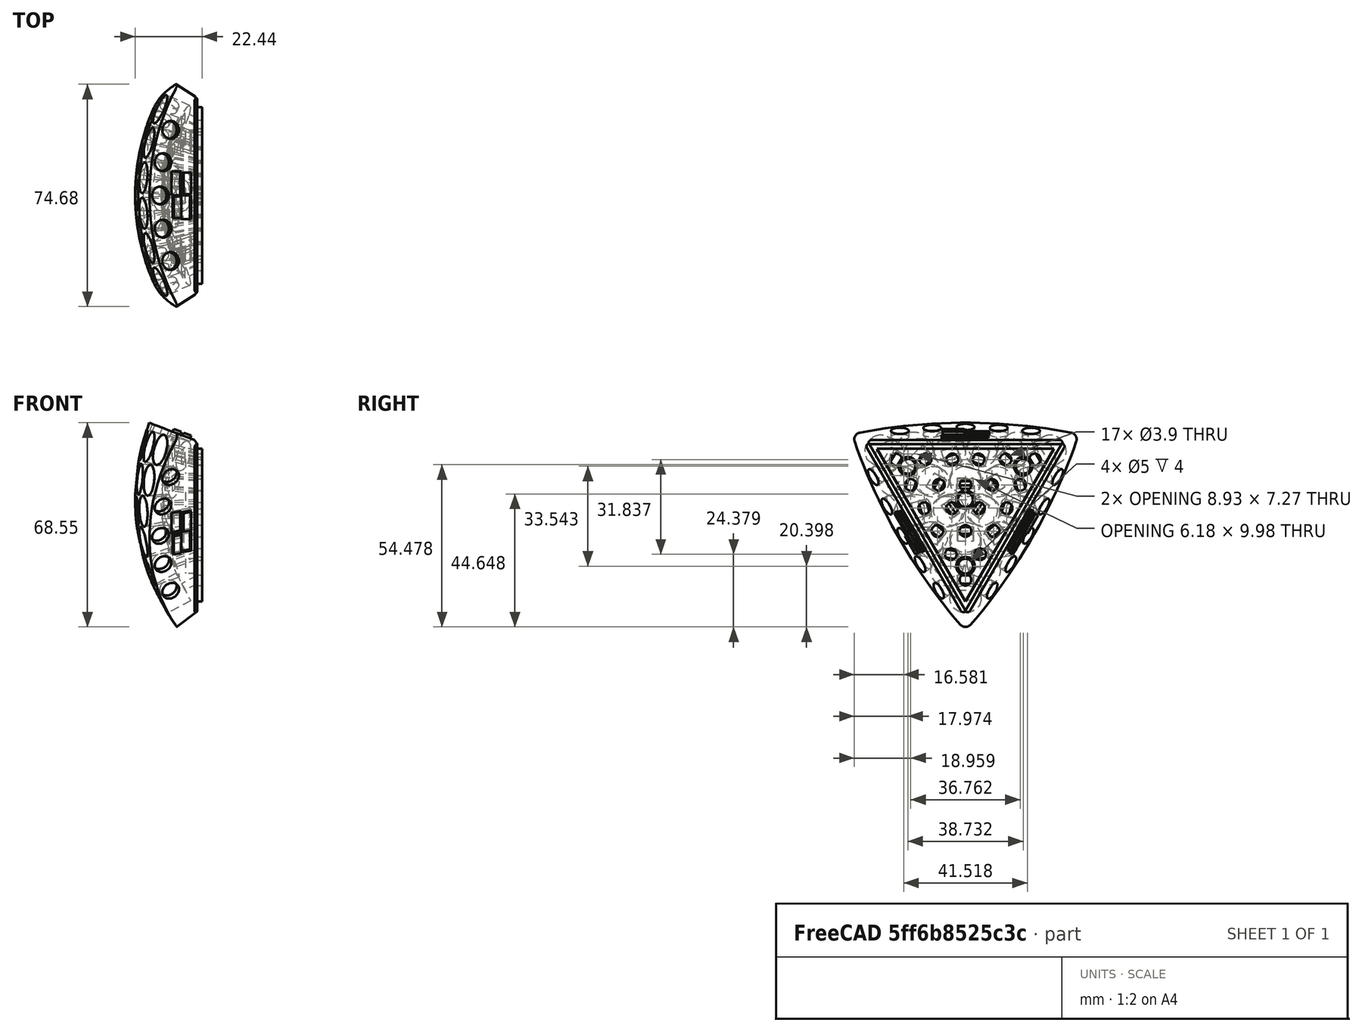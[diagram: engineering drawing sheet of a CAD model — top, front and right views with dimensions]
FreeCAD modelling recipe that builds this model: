
FCSTD DOCUMENT  (FreeCAD 0.20R26720 (Git))
Label: Shell_and_PCB_complete
License: All rights reserved
LicenseURL: http://en.wikipedia.org/wiki/All_rights_reserved
objects: App::FeaturePython×157, Part::FeaturePython×91, Part::Part2DObjectPython×22, App::Link×17, PartDesign::CoordinateSystem×13, Part::Feature×2, Part::Chamfer×1, Part::Fillet×1, PartDesign::FeatureBase×1, PartDesign::Body×1
note: 129 computed .brp shape members not serialized (recipe doc carries the construction recipe); baked Part::Feature solids carry a one-line shape summary decoded from their .brp

FEATURE [Part::Part2DObjectPython] Line  # Draft 2D object (typed FeaturePython)
  Area = 0
  ChamferSize = 0
  Closed = false
  End = (-64.0444,29.0183,16.7537)
  FilletRadius = 0
  Length = 72.2803
  MakeFace = true
  Points = (2) [(0,0,0),(-64.0444,29.0183,16.7537)]
  Start = (0,0,0)
  Subdivisions = 0
FEATURE [Part::Part2DObjectPython] Line001  # Draft 2D object (typed FeaturePython)
  Area = 0
  ChamferSize = 0
  Closed = false
  End = (-67.79,17.7334,17.7336)
  FilletRadius = 0
  Length = 72.2803
  MakeFace = true
  Points = (2) [(0,0,0),(-67.79,17.7334,17.7336)]
  Start = (0,0,0)
  Subdivisions = 0
FEATURE [Part::Part2DObjectPython] Line002  # Draft 2D object (typed FeaturePython)
  Area = 0
  ChamferSize = 0
  Closed = false
  End = (-69.6887,5.9653,18.2302)
  FilletRadius = 0
  Length = 72.2803
  MakeFace = true
  Points = (2) [(0,0,0),(-69.6887,5.9653,18.2302)]
  Start = (0,0,0)
  Subdivisions = 0
FEATURE [Part::Part2DObjectPython] Line003  # Draft 2D object (typed FeaturePython)
  Area = 0
  ChamferSize = 0
  Closed = false
  End = (-69.6887,-5.9653,18.2302)
  FilletRadius = 0
  Length = 72.2803
  MakeFace = true
  Points = (2) [(0,0,0),(-69.6887,-5.9653,18.2302)]
  Start = (0,0,0)
  Subdivisions = 0
FEATURE [Part::Part2DObjectPython] Line004  # Draft 2D object (typed FeaturePython)
  Area = 0
  ChamferSize = 0
  Closed = false
  End = (-67.79,-17.7334,17.7336)
  FilletRadius = 0
  Length = 72.2803
  MakeFace = true
  Points = (2) [(0,0,0),(-67.79,-17.7334,17.7336)]
  Start = (0,0,0)
  Subdivisions = 0
FEATURE [Part::Part2DObjectPython] Line005  # Draft 2D object (typed FeaturePython)
  Area = 0
  ChamferSize = 0
  Closed = false
  End = (-64.0444,-29.0183,16.7537)
  FilletRadius = 0
  Length = 72.2803
  MakeFace = true
  Points = (2) [(0,0,0),(-64.0444,-29.0183,16.7537)]
  Start = (0,0,0)
  Subdivisions = 0
FEATURE [Part::Part2DObjectPython] Line006  # Draft 2D object (typed FeaturePython)
  Area = 0
  ChamferSize = 0
  Closed = false
  End = (-67.79,24.2244,6.49078)
  FilletRadius = 0
  Length = 72.2803
  MakeFace = true
  Points = (2) [(0,0,0),(-67.79,24.2244,6.49078)]
  Start = (0,0,0)
  Subdivisions = 0
FEATURE [Part::Part2DObjectPython] Line007  # Draft 2D object (typed FeaturePython)
  Area = 0
  ChamferSize = 0
  Closed = false
  End = (-70.9033,12.2912,6.78887)
  FilletRadius = 0
  Length = 72.2803
  MakeFace = true
  Points = (2) [(0,0,0),(-70.9033,12.2912,6.78887)]
  Start = (0,0,0)
  Subdivisions = 0
FEATURE [Part::Part2DObjectPython] Line008  # Draft 2D object (typed FeaturePython)
  Area = 0
  ChamferSize = 0
  Closed = false
  End = (-71.9512,-1.03e-14,6.8892)
  FilletRadius = 0
  Length = 72.2803
  MakeFace = true
  Points = (2) [(0,0,0),(-71.9512,-1.02696e-14,6.8892)]
  Start = (0,0,0)
  Subdivisions = 0
FEATURE [Part::Part2DObjectPython] Line009  # Draft 2D object (typed FeaturePython)
  Area = 0
  ChamferSize = 0
  Closed = false
  End = (-70.9033,-12.2912,6.78887)
  FilletRadius = 0
  Length = 72.2803
  MakeFace = true
  Points = (2) [(0,0,0),(-70.9033,-12.2912,6.78887)]
  Start = (0,0,0)
  Subdivisions = 0
FEATURE [Part::Part2DObjectPython] Line010  # Draft 2D object (typed FeaturePython)
  Area = 0
  ChamferSize = 0
  Closed = false
  End = (-67.79,-24.2244,6.49078)
  FilletRadius = 0
  Length = 72.2803
  MakeFace = true
  Points = (2) [(0,0,0),(-67.79,-24.2244,6.49078)]
  Start = (0,0,0)
  Subdivisions = 0
FEATURE [Part::Part2DObjectPython] Line011  # Draft 2D object (typed FeaturePython)
  Area = 0
  ChamferSize = 0
  Closed = false
  End = (-69.6887,18.7705,-3.94902)
  FilletRadius = 0
  Length = 72.2803
  MakeFace = true
  Points = (2) [(0,0,0),(-69.6887,18.7705,-3.94902)]
  Start = (0,0,0)
  Subdivisions = 0
FEATURE [Part::Part2DObjectPython] Line012  # Draft 2D object (typed FeaturePython)
  Area = 0
  ChamferSize = 0
  Closed = false
  End = (-71.888,6.3213,-4.07365)
  FilletRadius = 0
  Length = 72.2803
  MakeFace = true
  Points = (2) [(0,0,0),(-71.888,6.3213,-4.07365)]
  Start = (0,0,0)
  Subdivisions = 0
FEATURE [Part::Part2DObjectPython] Line013  # Draft 2D object (typed FeaturePython)
  Area = 0
  ChamferSize = 0
  Closed = false
  End = (-71.888,-6.3213,-4.07365)
  FilletRadius = 0
  Length = 72.2803
  MakeFace = true
  Points = (2) [(0,0,0),(-71.888,-6.3213,-4.07365)]
  Start = (0,0,0)
  Subdivisions = 0
FEATURE [Part::Part2DObjectPython] Line014  # Draft 2D object (typed FeaturePython)
  Area = 0
  ChamferSize = 0
  Closed = false
  End = (-69.6887,-18.7705,-3.94902)
  FilletRadius = 0
  Length = 72.2803
  MakeFace = true
  Points = (2) [(0,0,0),(-69.6887,-18.7705,-3.94902)]
  Start = (0,0,0)
  Subdivisions = 0
FEATURE [Part::Part2DObjectPython] Line015  # Draft 2D object (typed FeaturePython)
  Area = 0
  ChamferSize = 0
  Closed = false
  End = (-69.6887,12.8052,-14.2812)
  FilletRadius = 0
  Length = 72.2803
  MakeFace = true
  Points = (2) [(0,0,0),(-69.6887,12.8052,-14.2812)]
  Start = (0,0,0)
  Subdivisions = 0
FEATURE [Part::Part2DObjectPython] Line016  # Draft 2D object (typed FeaturePython)
  Area = 0
  ChamferSize = 0
  Closed = false
  End = (-70.8088,7.7e-15,-14.5108)
  FilletRadius = 0
  Length = 72.2803
  MakeFace = true
  Points = (2) [(0,0,0),(-70.8088,7.66054e-15,-14.5108)]
  Start = (0,0,0)
  Subdivisions = 0
FEATURE [Part::Part2DObjectPython] Line017  # Draft 2D object (typed FeaturePython)
  Area = 0
  ChamferSize = 0
  Closed = false
  End = (-69.6887,-12.8052,-14.2812)
  FilletRadius = 0
  Length = 72.2803
  MakeFace = true
  Points = (2) [(0,0,0),(-69.6887,-12.8052,-14.2812)]
  Start = (0,0,0)
  Subdivisions = 0
FEATURE [Part::Part2DObjectPython] Line018  # Draft 2D object (typed FeaturePython)
  Area = 0
  ChamferSize = 0
  Closed = false
  End = (-67.79,6.49102,-24.2243)
  FilletRadius = 0
  Length = 72.2803
  MakeFace = true
  Points = (2) [(0,0,0),(-67.79,6.49102,-24.2243)]
  Start = (0,0,0)
  Subdivisions = 0
FEATURE [Part::Part2DObjectPython] Line019  # Draft 2D object (typed FeaturePython)
  Area = 0
  ChamferSize = 0
  Closed = false
  End = (-67.79,-6.49102,-24.2243)
  FilletRadius = 0
  Length = 72.2803
  MakeFace = true
  Points = (2) [(0,0,0),(-67.79,-6.49102,-24.2243)]
  Start = (0,0,0)
  Subdivisions = 0
FEATURE [Part::Part2DObjectPython] Line020  # Draft 2D object (typed FeaturePython)
  Area = 0
  ChamferSize = 0
  Closed = false
  End = (-64.0444,1.8e-15,-33.5075)
  FilletRadius = 0
  Length = 72.2803
  MakeFace = true
  Points = (2) [(0,0,0),(-64.0444,1.77636e-15,-33.5075)]
  Start = (0,0,0)
  Subdivisions = 0
FEATURE [Part::Part2DObjectPython] Line021  # Draft 2D object (typed FeaturePython)
  Area = 0
  ChamferSize = 0
  Closed = false
  End = (-57.4379,0,6.2e-15)
  FilletRadius = 0
  Length = 57.4379
  MakeFace = true
  Points = (2) [(0,0,0),(-57.4379,0,6.20075e-15)]
  Start = (0,0,0)
  Subdivisions = 0
FEATURE [Part::Feature] Shape
  shape: bbox 24.38 x 79.76 x 69.75 mm, 229 faces (baked)
FEATURE [Part::Feature] Shape001
  shape: bbox 1.6 x 59.35 x 51.4 mm, 36 faces (baked)
FEATURE [Part::Chamfer] Chamfer
  Base = -> Shape
  Edges = 3 edges r=1: [Edge26,Edge49,Edge72]
FEATURE [Part::Fillet] Fillet
  Base = -> Chamfer
  Edges = 3 edges r=2: [Edge1,Edge4,Edge27]
FEATURE [PartDesign::FeatureBase] BaseFeature
  BaseFeature = -> Fillet
FEATURE [PartDesign::CoordinateSystem] Local_CS
  AttacherType = Attacher::AttachEngine3D
  MapMode = 11
  Placement = pos=(-63.7856,-7e-15,24.3639) rot=(0.701166,0.701166,-0.129353;3.39887rad)
  Support = -> [BaseFeature]
FEATURE [PartDesign::CoordinateSystem] Local_CS001
  AttacherType = Attacher::AttachEngine3D
  MapMode = 11
  Placement = pos=(-63.7856,-21.0998,-12.182) rot=(-0.317298,-0.615291,-0.721622;1.68298rad)
  Support = -> [BaseFeature]
FEATURE [PartDesign::CoordinateSystem] Local_CS002
  AttacherType = Attacher::AttachEngine3D
  MapMode = 11
  Placement = pos=(-63.7856,21.0998,-12.182) rot=(0.544291,0.280684,-0.790546;2.00531rad)
  Support = -> [BaseFeature]
FEATURE [PartDesign::CoordinateSystem] Local_CS003
  AttacherType = Attacher::AttachEngine3D
  MapMode = 11
  Placement = pos=(-60.3757,8.95889,-30.6057) rot=(0.544291,0.280684,-0.790546;2.00531rad)
  Support = -> [BaseFeature]
FEATURE [PartDesign::CoordinateSystem] Local_CS004
  AttacherType = Attacher::AttachEngine3D
  MapMode = 11
  Placement = pos=(-60.3757,30.9848,7.54423) rot=(0.544291,0.280684,-0.790546;2.00531rad)
  Support = -> [BaseFeature]
FEATURE [PartDesign::CoordinateSystem] Local_CS005
  AttacherType = Attacher::AttachEngine3D
  MapMode = 11
  Placement = pos=(-60.3757,-8.95889,-30.6057) rot=(-0.317298,-0.615291,-0.721622;1.68298rad)
  Support = -> [BaseFeature]
FEATURE [PartDesign::CoordinateSystem] Local_CS006
  AttacherType = Attacher::AttachEngine3D
  MapMode = 11
  Placement = pos=(-60.3757,-30.9848,7.54423) rot=(-0.317298,-0.615291,-0.721622;1.68298rad)
  Support = -> [BaseFeature]
FEATURE [PartDesign::CoordinateSystem] Local_CS007
  AttacherType = Attacher::AttachEngine3D
  MapMode = 11
  Placement = pos=(-60.3757,-22.0259,23.0615) rot=(0.701166,0.701166,-0.129353;3.39887rad)
  Support = -> [BaseFeature]
FEATURE [PartDesign::CoordinateSystem] Local_CS008
  AttacherType = Attacher::AttachEngine3D
  MapMode = 11
  Placement = pos=(-60.3757,22.0259,23.0615) rot=(0.701166,0.701166,-0.129353;3.39887rad)
  Support = -> [BaseFeature]
FEATURE [PartDesign::CoordinateSystem] Local_CS009
  AttacherType = Attacher::AttachEngine3D
  MapMode = 11
  Placement = pos=(-51.4379,-19.3661,11.181) rot=(0.57735,0.57735,-0.57735;4.18879rad)
  Support = -> [BaseFeature]
FEATURE [PartDesign::CoordinateSystem] Local_CS010
  AttacherType = Attacher::AttachEngine3D
  MapMode = 11
  Placement = pos=(-51.4379,19.3661,11.181) rot=(0.57735,0.57735,-0.57735;4.18879rad)
  Support = -> [BaseFeature]
FEATURE [PartDesign::CoordinateSystem] Local_CS011
  AttacherType = Attacher::AttachEngine3D
  MapMode = 11
  Placement = pos=(-51.4379,0,-22.362) rot=(0.57735,0.57735,-0.57735;4.18879rad)
  Support = -> [BaseFeature]
FEATURE [PartDesign::CoordinateSystem] Local_CS012
  AttacherType = Attacher::AttachEngine3D
  MapMode = 11
  Placement = pos=(-51.4379,2e-15,1.69e-14) rot=(0.57735,0.57735,-0.57735;4.18879rad)
  Support = -> [BaseFeature]
FEATURE [PartDesign::Body] Body  label="shell"
  BaseFeature = -> Fillet
  Group = -> [BaseFeature,Local_CS,Local_CS001,Local_CS002,Local_CS003,Local_CS004,Local_CS005,Local_CS006,Local_CS007,Local_CS008,Local_CS009,Local_CS010,Local_CS011,Local_CS012]
  Origin = -> Origin
  Tip = -> BaseFeature
FEATURE [App::Link] Link  label="shell001"
  LinkedObject = -> Body
FEATURE [App::Link] Link001  label="shell002"
  LinkPlacement = pos=(7.7e-15,-5.52e-14,-1.103e-13) rot=(0.934172,-0.309017,0.178411;3.14159rad)
  LinkedObject = -> Body
  Placement = pos=(7.7e-15,-5.52e-14,-1.103e-13) rot=(0.934172,-0.309017,0.178411;3.14159rad)
FEATURE [App::Link] Link002  label="shell003"
  LinkPlacement = pos=(-1.36941e-09,6.11616e-09,3.09893e-09) rot=(0.794654,0.525731,-0.303531;1.25664rad)
  LinkedObject = -> Body
  Placement = pos=(-1.36941e-09,6.11616e-09,3.09893e-09) rot=(0.794654,0.525731,-0.303531;1.25664rad)
FEATURE [App::Link] Link003  label="shell004"
  LinkPlacement = pos=(-4.2003e-10,6.96406e-09,3.62865e-09) rot=(0.187592,0.850651,0.491123;1.25664rad)
  LinkedObject = -> Body
  Placement = pos=(-4.2003e-10,6.96406e-09,3.62865e-09) rot=(0.187592,0.850651,0.491123;1.25664rad)
FEATURE [App::Link] Link004  label="shell005"
  LinkPlacement = pos=(4.384e-12,-1.7666e-12,-5.0822e-12) rot=(0.745356,-0.57735,0.333333;2.0944rad)
  LinkedObject = -> Body
  Placement = pos=(4.384e-12,-1.7666e-12,-5.0822e-12) rot=(0.745356,-0.57735,0.333333;2.0944rad)
FEATURE [App::Link] Link005  label="shell006"
  LinkPlacement = pos=(-8.70131e-10,6.80711e-09,3.59799e-09) rot=(0.333333,0.934172,-0.127322;2.0944rad)
  LinkedObject = -> Body
  Placement = pos=(-8.70131e-10,6.80711e-09,3.59799e-09) rot=(0.333333,0.934172,-0.127322;2.0944rad)
FEATURE [App::Link] Link006  label="shell007"
  LinkPlacement = pos=(2.09781e-10,-2.78995e-11,-1.62592e-10) rot=(0.333333,-0.934172,-0.127322;2.0944rad)
  LinkedObject = -> Body
  Placement = pos=(2.09781e-10,-2.78995e-11,-1.62592e-10) rot=(0.333333,-0.934172,-0.127322;2.0944rad)
FEATURE [App::Link] Link007  label="shell008"
  LinkPlacement = pos=(-8.88912e-10,6.80266e-09,3.49688e-09) rot=(0.356822,0.809017,-0.467086;3.14159rad)
  LinkedObject = -> Body
  Placement = pos=(-8.88912e-10,6.80266e-09,3.49688e-09) rot=(0.356822,0.809017,-0.467086;3.14159rad)
FEATURE [App::Link] Link008  label="shell009"
  LinkPlacement = pos=(-5.90248e-10,-4.7757e-10,-1.80727e-09) rot=(0.356822,0,0.934172;3.14159rad)
  LinkedObject = -> Body
  Placement = pos=(-5.90248e-10,-4.7757e-10,-1.80727e-09) rot=(0.356822,0,0.934172;3.14159rad)
FEATURE [App::Link] Link009  label="shell010"
  LinkPlacement = pos=(-8.90973e-10,6.86674e-10,-1.59251e-09) rot=(0,-0.5,0.866025;3.14159rad)
  LinkedObject = -> Body
  Placement = pos=(-8.90973e-10,6.86674e-10,-1.59251e-09) rot=(0,-0.5,0.866025;3.14159rad)
FEATURE [Part::FeaturePython] Parts  # WARN: FeaturePython — macro-defined, semantics opaque (R4)
  Group = -> [Link001,Link,Link002,Link003,Link004,Link005,Link006,Link007,Link008,Link009]
  GroupMode = 0
FEATURE [App::Link] Link010  label="shell011"
  LinkPlacement = pos=(8.96105,1.2242e-07,11.0286) rot=(0,1,0;0.31747rad)
  LinkedObject = -> Body
  Placement = pos=(8.96105,1.2242e-07,11.0286) rot=(0,1,0;0.31747rad)
FEATURE [App::Link] Link011  label="shell012"
  LinkPlacement = pos=(8.96105,1.22409e-07,11.0286) rot=(0.654654,0.654654,-0.377965;1.44547rad)
  LinkedObject = -> Body
  Placement = pos=(8.96105,1.22409e-07,11.0286) rot=(0.654654,0.654654,-0.377965;1.44547rad)
FEATURE [App::Link] Link012  label="shell013"
  LinkPlacement = pos=(8.96105,1.22266e-07,11.0286) rot=(-0.816253,-0.334129,0.471264;1.11835rad)
  LinkedObject = -> Body
  Placement = pos=(8.96105,1.22266e-07,11.0286) rot=(-0.816253,-0.334129,0.471264;1.11835rad)
FEATURE [App::Link] Link013  label="shell014"
  LinkPlacement = pos=(8.96105,1.22267e-07,11.0286) rot=(-0.029286,0.21259,0.976702;1.29084rad)
  LinkedObject = -> Body
  Placement = pos=(8.96105,1.22267e-07,11.0286) rot=(-0.029286,0.21259,0.976702;1.29084rad)
FEATURE [App::Link] Link014  label="shell015"
  LinkPlacement = pos=(8.96105,1.22248e-07,11.0286) rot=(0.22258,0.895451,0.38552;1.53453rad)
  LinkedObject = -> Body
  Placement = pos=(8.96105,1.22248e-07,11.0286) rot=(0.22258,0.895451,0.38552;1.53453rad)
FEATURE [Part::FeaturePython] Parts001  # WARN: FeaturePython — macro-defined, semantics opaque (R4)
  Group = -> [Link010,Link011,Link012,Link013,Link014]
  GroupMode = 0
FEATURE [App::Link] Link015  label="Ring Assembly001"
  LinkPlacement = pos=(6.33641,-16.0136,1.7045) rot=(-0.868596,-0.489826,0.074905;0.379444rad)
  LinkedObject = -> Assembly
  Placement = pos=(6.33641,-16.0136,1.7045) rot=(-0.868596,-0.489826,0.074905;0.379444rad)
FEATURE [App::Link] Link016  label="Circle Assembly001"
  LinkPlacement = pos=(-8.99333e-06,-12.6957,-10.5744) rot=(0.678598,-0.281085,0.678598;1.09606rad)
  LinkedObject = -> Assembly001
  Placement = pos=(-8.99333e-06,-12.6957,-10.5744) rot=(0.678598,-0.281085,0.678598;1.09606rad)
FEATURE [Part::FeaturePython] Parts002  # WARN: FeaturePython — macro-defined, semantics opaque (R4)
  Group = -> [Link015,Link016]
  GroupMode = 0
FEATURE [Part::FeaturePython] Assembly  label="Ring Assembly"  # WARN: FeaturePython — macro-defined, semantics opaque (R4)
  AutoRelax = true
  BuildShape = 0
  Freeze = false
  Group = -> [Constraints,Elements,Parts]
  Verbose = false
  _SolverType = 1
  _Version = 1
FEATURE [App::FeaturePython] Constraints  # WARN: FeaturePython — macro-defined, semantics opaque (R4)
  Group = -> [Constraint,Constraint001,Constraint002,Constraint003,Constraint004,Constraint005,Constraint006,Constraint008,Constraint010,Constraint011,Constraint012,Constraint013,Constraint014,Constraint015,Constraint016,Constraint017,Constraint018,Constraint019,Constraint020,Constraint021,Constraint022,Constraint023,Constraint024,Constraint025,Constraint026,Constraint027,Constraint028,Constraint029,+6 more]
  _Version = 1
FEATURE [App::FeaturePython] Elements  # WARN: FeaturePython — macro-defined, semantics opaque (R4)
  Group = -> [_Element,_Element001,_Element002,_Element003,_Element004,_Element005,_Element006,_Element007,_Element008,_Element009,_Element010,_Element011,_Element012,_Element013,_Element015,_Element017,_Element019,_Element020,_Element021,_Element022,_Element023,_Element024,_Element025,_Element026,_Element027,_Element028,_Element029,_Element030,_Element031,_Element032,_Element033,_Element034,_Element035,+25 more]
FEATURE [App::FeaturePython] Constraint  label="AxialAlignment"  # WARN: FeaturePython — macro-defined, semantics opaque (R4)
  Angle = 0
  AnglePitch = 0
  AngleRoll = 0
  Disabled = false
  Group = -> [ElementLink,ElementLink001]
  LockAngle = false
  Multiply = false
  _ConstraintType = 36
  _Parent = -> Constraints
FEATURE [App::FeaturePython] ElementLink  label="_Element"  # link proxy (typed FeaturePython)
  LinkTransform = true
  LinkedObject = -> _Element
  _Parent = -> Constraint
FEATURE [Part::FeaturePython] _Element  # link proxy (typed FeaturePython)
  Detach = false
  LinkTransform = true
  LinkedObject = -> Link [BaseFeature.Edge218]
  _Parent = -> Elements
FEATURE [App::FeaturePython] ElementLink001  label="_Element001"  # link proxy (typed FeaturePython)
  LinkTransform = true
  LinkedObject = -> _Element001
  _Parent = -> Constraint
FEATURE [Part::FeaturePython] _Element001  # link proxy (typed FeaturePython)
  Detach = false
  LinkTransform = true
  LinkedObject = -> Link001 [BaseFeature.Edge198]
  _Parent = -> Elements
FEATURE [App::FeaturePython] Constraint001  label="AxialAlignment001"  # WARN: FeaturePython — macro-defined, semantics opaque (R4)
  Angle = 0
  AnglePitch = 0
  AngleRoll = 0
  Disabled = false
  Group = -> [ElementLink002,ElementLink003]
  LockAngle = false
  Multiply = false
  _ConstraintType = 36
  _Parent = -> Constraints
FEATURE [App::FeaturePython] ElementLink002  label="_Element002"  # link proxy (typed FeaturePython)
  LinkTransform = true
  LinkedObject = -> _Element002
  _Parent = -> Constraint001
FEATURE [Part::FeaturePython] _Element002  # link proxy (typed FeaturePython)
  Detach = false
  LinkTransform = true
  LinkedObject = -> Link [BaseFeature.Edge198]
  _Parent = -> Elements
FEATURE [App::FeaturePython] ElementLink003  label="_Element003"  # link proxy (typed FeaturePython)
  LinkTransform = true
  LinkedObject = -> _Element003
  _Parent = -> Constraint001
FEATURE [Part::FeaturePython] _Element003  # link proxy (typed FeaturePython)
  Detach = false
  LinkTransform = true
  LinkedObject = -> Link001 [BaseFeature.Edge218]
  _Parent = -> Elements
FEATURE [Part::FeaturePython] _Element004  # link proxy (typed FeaturePython)
  Detach = false
  LinkTransform = true
  LinkedObject = -> Link001 [BaseFeature.Face30]
  _Parent = -> Elements
FEATURE [Part::FeaturePython] _Element005  # link proxy (typed FeaturePython)
  Detach = false
  LinkTransform = true
  LinkedObject = -> Link [BaseFeature.Face30]
  _Parent = -> Elements
FEATURE [App::FeaturePython] Constraint002  label="PlaneCoincident"  # WARN: FeaturePython — macro-defined, semantics opaque (R4)
  Angle = 0
  AnglePitch = 0
  AngleRoll = 0
  Cascade = false
  Disabled = false
  Group = -> [ElementLink004,ElementLink005]
  LockAngle = false
  Multiply = false
  OffsetX = 0
  OffsetY = 0
  _ConstraintType = 35
  _Parent = -> Constraints
FEATURE [App::FeaturePython] ElementLink004  label="_Element006"  # link proxy (typed FeaturePython)
  LinkTransform = true
  LinkedObject = -> _Element006
  _Parent = -> Constraint002
FEATURE [Part::FeaturePython] _Element006  # link proxy (typed FeaturePython)
  Detach = false
  LinkTransform = true
  LinkedObject = -> Link [BaseFeature.Edge209]
  _Parent = -> Elements
FEATURE [App::FeaturePython] ElementLink005  label="_Element007"  # link proxy (typed FeaturePython)
  LinkTransform = true
  LinkedObject = -> _Element007
  _Parent = -> Constraint002
FEATURE [Part::FeaturePython] _Element007  # link proxy (typed FeaturePython)
  Detach = false
  LinkTransform = true
  LinkedObject = -> Link001 [BaseFeature.Edge199]
  _Parent = -> Elements
FEATURE [App::FeaturePython] Constraint003  label="AxialAlignment002"  # WARN: FeaturePython — macro-defined, semantics opaque (R4)
  Angle = 0
  AnglePitch = 0
  AngleRoll = 0
  Disabled = true
  Group = -> [ElementLink006,ElementLink007]
  LockAngle = false
  Multiply = false
  _ConstraintType = 36
  _Parent = -> Constraints
FEATURE [App::FeaturePython] ElementLink006  label="_Element008"  # link proxy (typed FeaturePython)
  LinkTransform = true
  LinkedObject = -> _Element008
  _Parent = -> Constraint003
FEATURE [Part::FeaturePython] _Element008  # link proxy (typed FeaturePython)
  Detach = false
  LinkTransform = true
  LinkedObject = -> Link [BaseFeature.Edge240]
  _Parent = -> Elements
FEATURE [App::FeaturePython] ElementLink007  label="_Element009"  # link proxy (typed FeaturePython)
  LinkTransform = true
  LinkedObject = -> _Element009
  _Parent = -> Constraint003
FEATURE [Part::FeaturePython] _Element009  # link proxy (typed FeaturePython)
  Detach = false
  LinkTransform = true
  LinkedObject = -> Link002 [BaseFeature.Edge17]
  _Parent = -> Elements
FEATURE [App::FeaturePython] Constraint004  label="AxialAlignment003"  # WARN: FeaturePython — macro-defined, semantics opaque (R4)
  Angle = 0
  AnglePitch = 0
  AngleRoll = 0
  Disabled = true
  Group = -> [ElementLink008,ElementLink009]
  LockAngle = false
  Multiply = false
  _ConstraintType = 36
  _Parent = -> Constraints
FEATURE [App::FeaturePython] ElementLink008  label="_Element010"  # link proxy (typed FeaturePython)
  LinkTransform = true
  LinkedObject = -> _Element010
  _Parent = -> Constraint004
FEATURE [Part::FeaturePython] _Element010  # link proxy (typed FeaturePython)
  Detach = false
  LinkTransform = true
  LinkedObject = -> Link002 [BaseFeature.Edge6]
  _Parent = -> Elements
FEATURE [App::FeaturePython] ElementLink009  label="_Element011"  # link proxy (typed FeaturePython)
  LinkTransform = true
  LinkedObject = -> _Element011
  _Parent = -> Constraint004
FEATURE [Part::FeaturePython] _Element011  # link proxy (typed FeaturePython)
  Detach = false
  LinkTransform = true
  LinkedObject = -> Link [BaseFeature.Edge239]
  _Parent = -> Elements
FEATURE [App::FeaturePython] Constraint005  label="AxialAlignment004"  # WARN: FeaturePython — macro-defined, semantics opaque (R4)
  Angle = 0
  AnglePitch = 0
  AngleRoll = 0
  Disabled = true
  Group = -> [ElementLink010,ElementLink011]
  LockAngle = false
  Multiply = false
  _ConstraintType = 36
  _Parent = -> Constraints
FEATURE [App::FeaturePython] ElementLink010  label="_Element012"  # link proxy (typed FeaturePython)
  LinkTransform = true
  LinkedObject = -> _Element012
  _Parent = -> Constraint005
FEATURE [Part::FeaturePython] _Element012  # link proxy (typed FeaturePython)
  Detach = false
  LinkTransform = true
  LinkedObject = -> Link002 [BaseFeature.Edge7]
  _Parent = -> Elements
FEATURE [App::FeaturePython] ElementLink011  label="_Element013"  # link proxy (typed FeaturePython)
  LinkTransform = true
  LinkedObject = -> _Element013
  _Parent = -> Constraint005
FEATURE [Part::FeaturePython] _Element013  # link proxy (typed FeaturePython)
  Detach = false
  LinkTransform = true
  LinkedObject = -> Link [BaseFeature.Edge228]
  _Parent = -> Elements
FEATURE [App::FeaturePython] Constraint006  label="PlaneCoincident001"  # WARN: FeaturePython — macro-defined, semantics opaque (R4)
  Angle = 0
  AnglePitch = 0
  AngleRoll = 0
  Cascade = false
  Disabled = true
  Group = -> [ElementLink012,ElementLink013]
  LockAngle = false
  Multiply = false
  OffsetX = 0
  OffsetY = 0
  _ConstraintType = 35
  _Parent = -> Constraints
FEATURE [App::FeaturePython] ElementLink012  label="_Element013"  # link proxy (typed FeaturePython)
  LinkTransform = true
  LinkedObject = -> _Element013
  _Parent = -> Constraint006
FEATURE [App::FeaturePython] ElementLink013  label="_Element012"  # link proxy (typed FeaturePython)
  LinkTransform = true
  LinkedObject = -> _Element012
  _Parent = -> Constraint006
FEATURE [Part::FeaturePython] _Element015  # link proxy (typed FeaturePython)
  Detach = false
  LinkTransform = true
  LinkedObject = -> Link002 [BaseFeature.Edge228]
  _Parent = -> Elements
FEATURE [Part::FeaturePython] _Element017  # link proxy (typed FeaturePython)
  Detach = false
  LinkTransform = true
  LinkedObject = -> Link002 [BaseFeature.Edge240]
  _Parent = -> Elements
FEATURE [Part::FeaturePython] _Element019  # link proxy (typed FeaturePython)
  Detach = false
  LinkTransform = true
  LinkedObject = -> Link002 [BaseFeature.Edge239]
  _Parent = -> Elements
FEATURE [Part::FeaturePython] _Element020  # link proxy (typed FeaturePython)
  Detach = false
  LinkTransform = true
  LinkedObject = -> Link003 [BaseFeature.Edge198]
  _Parent = -> Elements
FEATURE [App::FeaturePython] Constraint008  label="Locked"  # WARN: FeaturePython — macro-defined, semantics opaque (R4)
  Disabled = false
  Group = -> [ElementLink016,ElementLink017,ElementLink018]
  _ConstraintType = 0
  _Parent = -> Constraints
FEATURE [App::FeaturePython] ElementLink016  label="_Element021"  # link proxy (typed FeaturePython)
  LinkTransform = true
  LinkedObject = -> _Element021
  _Parent = -> Constraint008
FEATURE [Part::FeaturePython] _Element021  # link proxy (typed FeaturePython)
  Detach = false
  LinkTransform = true
  LinkedObject = -> Link002 [BaseFeature.Face31]
  _Parent = -> Elements
FEATURE [App::FeaturePython] ElementLink017  label="_Element022"  # link proxy (typed FeaturePython)
  LinkTransform = true
  LinkedObject = -> _Element022
  _Parent = -> Constraint008
FEATURE [Part::FeaturePython] _Element022  # link proxy (typed FeaturePython)
  Detach = false
  LinkTransform = true
  LinkedObject = -> Link [BaseFeature.Face1]
  _Parent = -> Elements
FEATURE [App::FeaturePython] ElementLink018  label="_Element023"  # link proxy (typed FeaturePython)
  LinkTransform = true
  LinkedObject = -> _Element023
  _Parent = -> Constraint008
FEATURE [Part::FeaturePython] _Element023  # link proxy (typed FeaturePython)
  Detach = false
  LinkTransform = true
  LinkedObject = -> Link001 [BaseFeature.Face31]
  _Parent = -> Elements
FEATURE [Part::FeaturePython] _Element024  # link proxy (typed FeaturePython)
  Detach = false
  LinkTransform = true
  LinkedObject = -> Link003 [BaseFeature.Edge218]
  _Parent = -> Elements
FEATURE [App::FeaturePython] Constraint010  label="PlaneCoincident002"  # WARN: FeaturePython — macro-defined, semantics opaque (R4)
  Angle = 0
  AnglePitch = 0
  AngleRoll = 0
  Cascade = false
  Disabled = false
  Group = -> [ElementLink021,ElementLink022]
  LockAngle = false
  Multiply = false
  OffsetX = 0
  OffsetY = 0
  _ConstraintType = 35
  _Parent = -> Constraints
FEATURE [App::FeaturePython] ElementLink021  label="_Element024"  # link proxy (typed FeaturePython)
  LinkTransform = true
  LinkedObject = -> _Element024
  _Parent = -> Constraint010
FEATURE [App::FeaturePython] ElementLink022  label="_Element017"  # link proxy (typed FeaturePython)
  LinkTransform = true
  LinkedObject = -> _Element017
  _Parent = -> Constraint010
FEATURE [App::FeaturePython] Constraint011  label="Locked001"  # WARN: FeaturePython — macro-defined, semantics opaque (R4)
  Disabled = false
  Group = -> [ElementLink023]
  _ConstraintType = 0
  _Parent = -> Constraints
FEATURE [App::FeaturePython] ElementLink023  label="_Element025"  # link proxy (typed FeaturePython)
  LinkTransform = true
  LinkedObject = -> _Element025
  _Parent = -> Constraint011
FEATURE [Part::FeaturePython] _Element025  # link proxy (typed FeaturePython)
  Detach = false
  LinkTransform = true
  LinkedObject = -> Link003 [BaseFeature.Face5]
  _Parent = -> Elements
FEATURE [Part::FeaturePython] _Element026  # link proxy (typed FeaturePython)
  Detach = false
  LinkTransform = true
  LinkedObject = -> Link004 [BaseFeature.Edge7]
  _Parent = -> Elements
FEATURE [Part::FeaturePython] _Element027  # link proxy (typed FeaturePython)
  Detach = false
  LinkTransform = true
  LinkedObject = -> Link001 [BaseFeature.Edge228]
  _Parent = -> Elements
FEATURE [Part::FeaturePython] _Element028  # link proxy (typed FeaturePython)
  Detach = false
  LinkTransform = true
  LinkedObject = -> Link004 [BaseFeature.Edge6]
  _Parent = -> Elements
FEATURE [Part::FeaturePython] _Element029  # link proxy (typed FeaturePython)
  Detach = false
  LinkTransform = true
  LinkedObject = -> Link001 [BaseFeature.Edge239]
  _Parent = -> Elements
FEATURE [App::FeaturePython] Constraint012  label="AxialAlignment005"  # WARN: FeaturePython — macro-defined, semantics opaque (R4)
  Angle = 0
  AnglePitch = 0
  AngleRoll = 0
  Disabled = true
  Group = -> [ElementLink024,ElementLink025]
  LockAngle = false
  Multiply = false
  _ConstraintType = 36
  _Parent = -> Constraints
FEATURE [App::FeaturePython] ElementLink024  label="_Element030"  # link proxy (typed FeaturePython)
  LinkTransform = true
  LinkedObject = -> _Element030
  _Parent = -> Constraint012
FEATURE [Part::FeaturePython] _Element030  # link proxy (typed FeaturePython)
  Detach = false
  LinkTransform = true
  LinkedObject = -> Link004 [BaseFeature.Edge208]
  _Parent = -> Elements
FEATURE [App::FeaturePython] ElementLink025  label="_Element029"  # link proxy (typed FeaturePython)
  LinkTransform = true
  LinkedObject = -> _Element029
  _Parent = -> Constraint012
FEATURE [App::FeaturePython] Constraint013  label="AxialAlignment006"  # WARN: FeaturePython — macro-defined, semantics opaque (R4)
  Angle = 0
  AnglePitch = 0
  AngleRoll = 0
  Disabled = true
  Group = -> [ElementLink026,ElementLink027]
  LockAngle = false
  Multiply = false
  _ConstraintType = 36
  _Parent = -> Constraints
FEATURE [App::FeaturePython] ElementLink026  label="_Element031"  # link proxy (typed FeaturePython)
  LinkTransform = true
  LinkedObject = -> _Element031
  _Parent = -> Constraint013
FEATURE [Part::FeaturePython] _Element031  # link proxy (typed FeaturePython)
  Detach = false
  LinkTransform = true
  LinkedObject = -> Link004 [BaseFeature.Edge198]
  _Parent = -> Elements
FEATURE [App::FeaturePython] ElementLink027  label="_Element027"  # link proxy (typed FeaturePython)
  LinkTransform = true
  LinkedObject = -> _Element027
  _Parent = -> Constraint013
FEATURE [App::FeaturePython] Constraint014  label="PlaneCoincident003"  # WARN: FeaturePython — macro-defined, semantics opaque (R4)
  Angle = 0
  AnglePitch = 0
  AngleRoll = 0
  Cascade = false
  Disabled = false
  Group = -> [ElementLink028,ElementLink029]
  LockAngle = false
  Multiply = false
  OffsetX = 0
  OffsetY = 0
  _ConstraintType = 35
  _Parent = -> Constraints
FEATURE [App::FeaturePython] ElementLink028  label="_Element027"  # link proxy (typed FeaturePython)
  LinkTransform = true
  LinkedObject = -> _Element027
  _Parent = -> Constraint014
FEATURE [App::FeaturePython] ElementLink029  label="_Element031"  # link proxy (typed FeaturePython)
  LinkTransform = true
  LinkedObject = -> _Element031
  _Parent = -> Constraint014
FEATURE [App::FeaturePython] Constraint015  label="Locked002"  # WARN: FeaturePython — macro-defined, semantics opaque (R4)
  Disabled = false
  Group = -> [ElementLink030]
  _ConstraintType = 0
  _Parent = -> Constraints
FEATURE [App::FeaturePython] ElementLink030  label="_Element032"  # link proxy (typed FeaturePython)
  LinkTransform = true
  LinkedObject = -> _Element032
  _Parent = -> Constraint015
FEATURE [Part::FeaturePython] _Element032  # link proxy (typed FeaturePython)
  Detach = false
  LinkTransform = true
  LinkedObject = -> Link004 [BaseFeature.Face1]
  _Parent = -> Elements
FEATURE [App::FeaturePython] Constraint016  label="AxialAlignment007"  # WARN: FeaturePython — macro-defined, semantics opaque (R4)
  Angle = 0
  AnglePitch = 0
  AngleRoll = 0
  Disabled = true
  Group = -> [ElementLink031,ElementLink032]
  LockAngle = false
  Multiply = false
  _ConstraintType = 36
  _Parent = -> Constraints
FEATURE [App::FeaturePython] ElementLink031  label="_Element033"  # link proxy (typed FeaturePython)
  LinkTransform = true
  LinkedObject = -> _Element033
  _Parent = -> Constraint016
FEATURE [Part::FeaturePython] _Element033  # link proxy (typed FeaturePython)
  Detach = false
  LinkTransform = true
  LinkedObject = -> Link003 [BaseFeature.Edge228]
  _Parent = -> Elements
FEATURE [App::FeaturePython] ElementLink032  label="_Element034"  # link proxy (typed FeaturePython)
  LinkTransform = true
  LinkedObject = -> _Element034
  _Parent = -> Constraint016
FEATURE [Part::FeaturePython] _Element034  # link proxy (typed FeaturePython)
  Detach = false
  LinkTransform = true
  LinkedObject = -> Link005 [BaseFeature.Edge7]
  _Parent = -> Elements
FEATURE [App::FeaturePython] Constraint017  label="AxialAlignment008"  # WARN: FeaturePython — macro-defined, semantics opaque (R4)
  Angle = 0
  AnglePitch = 0
  AngleRoll = 0
  Disabled = true
  Group = -> [ElementLink033,ElementLink034]
  LockAngle = false
  Multiply = false
  _ConstraintType = 36
  _Parent = -> Constraints
FEATURE [App::FeaturePython] ElementLink033  label="_Element035"  # link proxy (typed FeaturePython)
  LinkTransform = true
  LinkedObject = -> _Element035
  _Parent = -> Constraint017
FEATURE [Part::FeaturePython] _Element035  # link proxy (typed FeaturePython)
  Detach = false
  LinkTransform = true
  LinkedObject = -> Link005 [BaseFeature.Edge6]
  _Parent = -> Elements
FEATURE [App::FeaturePython] ElementLink034  label="_Element036"  # link proxy (typed FeaturePython)
  LinkTransform = true
  LinkedObject = -> _Element036
  _Parent = -> Constraint017
FEATURE [Part::FeaturePython] _Element036  # link proxy (typed FeaturePython)
  Detach = false
  LinkTransform = true
  LinkedObject = -> Link003 [BaseFeature.Edge239]
  _Parent = -> Elements
FEATURE [App::FeaturePython] Constraint018  label="PlaneCoincident004"  # WARN: FeaturePython — macro-defined, semantics opaque (R4)
  Angle = 0
  AnglePitch = 0
  AngleRoll = 0
  Cascade = false
  Disabled = false
  Group = -> [ElementLink035,ElementLink036]
  LockAngle = false
  Multiply = false
  OffsetX = 0
  OffsetY = 0
  _ConstraintType = 35
  _Parent = -> Constraints
FEATURE [App::FeaturePython] ElementLink035  label="_Element037"  # link proxy (typed FeaturePython)
  LinkTransform = true
  LinkedObject = -> _Element037
  _Parent = -> Constraint018
FEATURE [Part::FeaturePython] _Element037  # link proxy (typed FeaturePython)
  Detach = false
  LinkTransform = true
  LinkedObject = -> Link003 [BaseFeature.Edge240]
  _Parent = -> Elements
FEATURE [App::FeaturePython] ElementLink036  label="_Element038"  # link proxy (typed FeaturePython)
  LinkTransform = true
  LinkedObject = -> _Element038
  _Parent = -> Constraint018
FEATURE [Part::FeaturePython] _Element038  # link proxy (typed FeaturePython)
  Detach = false
  LinkTransform = true
  LinkedObject = -> Link005 [BaseFeature.Edge17]
  _Parent = -> Elements
FEATURE [App::FeaturePython] Constraint019  label="AxialAlignment009"  # WARN: FeaturePython — macro-defined, semantics opaque (R4)
  Angle = 0
  AnglePitch = 0
  AngleRoll = 0
  Disabled = true
  Group = -> [ElementLink037,ElementLink038]
  LockAngle = false
  Multiply = false
  _ConstraintType = 36
  _Parent = -> Constraints
FEATURE [App::FeaturePython] ElementLink037  label="_Element039"  # link proxy (typed FeaturePython)
  LinkTransform = true
  LinkedObject = -> _Element039
  _Parent = -> Constraint019
FEATURE [Part::FeaturePython] _Element039  # link proxy (typed FeaturePython)
  Detach = false
  LinkTransform = true
  LinkedObject = -> Link006 [BaseFeature.Edge228]
  _Parent = -> Elements
FEATURE [App::FeaturePython] ElementLink038  label="_Element026"  # link proxy (typed FeaturePython)
  LinkTransform = true
  LinkedObject = -> _Element026
  _Parent = -> Constraint019
FEATURE [App::FeaturePython] Constraint020  label="Locked003"  # WARN: FeaturePython — macro-defined, semantics opaque (R4)
  Disabled = false
  Group = -> [ElementLink039]
  _ConstraintType = 0
  _Parent = -> Constraints
FEATURE [App::FeaturePython] ElementLink039  label="_Element040"  # link proxy (typed FeaturePython)
  LinkTransform = true
  LinkedObject = -> _Element040
  _Parent = -> Constraint020
FEATURE [Part::FeaturePython] _Element040  # link proxy (typed FeaturePython)
  Detach = false
  LinkTransform = true
  LinkedObject = -> Link005 [BaseFeature.Face31]
  _Parent = -> Elements
FEATURE [App::FeaturePython] Constraint021  label="AxialAlignment010"  # WARN: FeaturePython — macro-defined, semantics opaque (R4)
  Angle = 0
  AnglePitch = 0
  AngleRoll = 0
  Disabled = true
  Group = -> [ElementLink040,ElementLink041]
  LockAngle = false
  Multiply = false
  _ConstraintType = 36
  _Parent = -> Constraints
FEATURE [App::FeaturePython] ElementLink040  label="_Element041"  # link proxy (typed FeaturePython)
  LinkTransform = true
  LinkedObject = -> _Element041
  _Parent = -> Constraint021
FEATURE [Part::FeaturePython] _Element041  # link proxy (typed FeaturePython)
  Detach = false
  LinkTransform = true
  LinkedObject = -> Link006 [BaseFeature.Edge240]
  _Parent = -> Elements
FEATURE [App::FeaturePython] ElementLink041  label="_Element042"  # link proxy (typed FeaturePython)
  LinkTransform = true
  LinkedObject = -> _Element042
  _Parent = -> Constraint021
FEATURE [Part::FeaturePython] _Element042  # link proxy (typed FeaturePython)
  Detach = false
  LinkTransform = true
  LinkedObject = -> Link004 [BaseFeature.Edge17]
  _Parent = -> Elements
FEATURE [App::FeaturePython] Constraint022  label="PlaneCoincident005"  # WARN: FeaturePython — macro-defined, semantics opaque (R4)
  Angle = 0
  AnglePitch = 0
  AngleRoll = 0
  Cascade = false
  Disabled = false
  Group = -> [ElementLink042,ElementLink043]
  LockAngle = false
  Multiply = false
  OffsetX = 0
  OffsetY = 0
  _ConstraintType = 35
  _Parent = -> Constraints
FEATURE [App::FeaturePython] ElementLink042  label="_Element042"  # link proxy (typed FeaturePython)
  LinkTransform = true
  LinkedObject = -> _Element042
  _Parent = -> Constraint022
FEATURE [App::FeaturePython] ElementLink043  label="_Element041"  # link proxy (typed FeaturePython)
  LinkTransform = true
  LinkedObject = -> _Element041
  _Parent = -> Constraint022
FEATURE [App::FeaturePython] Constraint023  label="Locked004"  # WARN: FeaturePython — macro-defined, semantics opaque (R4)
  Disabled = false
  Group = -> [ElementLink044]
  _ConstraintType = 0
  _Parent = -> Constraints
FEATURE [App::FeaturePython] ElementLink044  label="_Element043"  # link proxy (typed FeaturePython)
  LinkTransform = true
  LinkedObject = -> _Element043
  _Parent = -> Constraint023
FEATURE [Part::FeaturePython] _Element043  # link proxy (typed FeaturePython)
  Detach = false
  LinkTransform = true
  LinkedObject = -> Link006 [BaseFeature.Face5]
  _Parent = -> Elements
FEATURE [App::FeaturePython] Constraint024  label="AxialAlignment011"  # WARN: FeaturePython — macro-defined, semantics opaque (R4)
  Angle = 0
  AnglePitch = 0
  AngleRoll = 0
  Disabled = true
  Group = -> [ElementLink045,ElementLink046]
  LockAngle = false
  Multiply = false
  _ConstraintType = 36
  _Parent = -> Constraints
FEATURE [App::FeaturePython] ElementLink045  label="_Element044"  # link proxy (typed FeaturePython)
  LinkTransform = true
  LinkedObject = -> _Element044
  _Parent = -> Constraint024
FEATURE [Part::FeaturePython] _Element044  # link proxy (typed FeaturePython)
  Detach = false
  LinkTransform = true
  LinkedObject = -> Link007 [BaseFeature.Edge7]
  _Parent = -> Elements
FEATURE [App::FeaturePython] ElementLink046  label="_Element045"  # link proxy (typed FeaturePython)
  LinkTransform = true
  LinkedObject = -> _Element045
  _Parent = -> Constraint024
FEATURE [Part::FeaturePython] _Element045  # link proxy (typed FeaturePython)
  Detach = false
  LinkTransform = true
  LinkedObject = -> Link005 [BaseFeature.Edge228]
  _Parent = -> Elements
FEATURE [App::FeaturePython] Constraint025  label="AxialAlignment012"  # WARN: FeaturePython — macro-defined, semantics opaque (R4)
  Angle = 0
  AnglePitch = 0
  AngleRoll = 0
  Disabled = true
  Group = -> [ElementLink047,ElementLink048]
  LockAngle = false
  Multiply = false
  _ConstraintType = 36
  _Parent = -> Constraints
FEATURE [App::FeaturePython] ElementLink047  label="_Element046"  # link proxy (typed FeaturePython)
  LinkTransform = true
  LinkedObject = -> _Element046
  _Parent = -> Constraint025
FEATURE [Part::FeaturePython] _Element046  # link proxy (typed FeaturePython)
  Detach = false
  LinkTransform = true
  LinkedObject = -> Link005 [BaseFeature.Edge240]
  _Parent = -> Elements
FEATURE [App::FeaturePython] ElementLink048  label="_Element047"  # link proxy (typed FeaturePython)
  LinkTransform = true
  LinkedObject = -> _Element047
  _Parent = -> Constraint025
FEATURE [Part::FeaturePython] _Element047  # link proxy (typed FeaturePython)
  Detach = false
  LinkTransform = true
  LinkedObject = -> Link007 [BaseFeature.Edge17]
  _Parent = -> Elements
FEATURE [App::FeaturePython] Constraint026  label="PlaneCoincident006"  # WARN: FeaturePython — macro-defined, semantics opaque (R4)
  Angle = 0
  AnglePitch = 0
  AngleRoll = 0
  Cascade = false
  Disabled = false
  Group = -> [ElementLink049,ElementLink050]
  LockAngle = false
  Multiply = false
  OffsetX = 0
  OffsetY = 0
  _ConstraintType = 35
  _Parent = -> Constraints
FEATURE [App::FeaturePython] ElementLink049  label="_Element047"  # link proxy (typed FeaturePython)
  LinkTransform = true
  LinkedObject = -> _Element047
  _Parent = -> Constraint026
FEATURE [App::FeaturePython] ElementLink050  label="_Element046"  # link proxy (typed FeaturePython)
  LinkTransform = true
  LinkedObject = -> _Element046
  _Parent = -> Constraint026
FEATURE [App::FeaturePython] Constraint027  label="Locked005"  # WARN: FeaturePython — macro-defined, semantics opaque (R4)
  Disabled = false
  Group = -> [ElementLink051]
  _ConstraintType = 0
  _Parent = -> Constraints
FEATURE [App::FeaturePython] ElementLink051  label="_Element048"  # link proxy (typed FeaturePython)
  LinkTransform = true
  LinkedObject = -> _Element048
  _Parent = -> Constraint027
FEATURE [Part::FeaturePython] _Element048  # link proxy (typed FeaturePython)
  Detach = false
  LinkTransform = true
  LinkedObject = -> Link007 [BaseFeature.Face5]
  _Parent = -> Elements
FEATURE [App::FeaturePython] Constraint028  label="AxialAlignment013"  # WARN: FeaturePython — macro-defined, semantics opaque (R4)
  Angle = 0
  AnglePitch = 0
  AngleRoll = 0
  Disabled = true
  Group = -> [ElementLink052,ElementLink053]
  LockAngle = false
  Multiply = false
  _ConstraintType = 36
  _Parent = -> Constraints
FEATURE [App::FeaturePython] ElementLink052  label="_Element049"  # link proxy (typed FeaturePython)
  LinkTransform = true
  LinkedObject = -> _Element049
  _Parent = -> Constraint028
FEATURE [Part::FeaturePython] _Element049  # link proxy (typed FeaturePython)
  Detach = false
  LinkTransform = true
  LinkedObject = -> Link006 [BaseFeature.Edge7]
  _Parent = -> Elements
FEATURE [App::FeaturePython] ElementLink053  label="_Element050"  # link proxy (typed FeaturePython)
  LinkTransform = true
  LinkedObject = -> _Element050
  _Parent = -> Constraint028
FEATURE [Part::FeaturePython] _Element050  # link proxy (typed FeaturePython)
  Detach = false
  LinkTransform = true
  LinkedObject = -> Link008 [BaseFeature.Edge17]
  _Parent = -> Elements
FEATURE [App::FeaturePython] Constraint029  label="AxialAlignment014"  # WARN: FeaturePython — macro-defined, semantics opaque (R4)
  Angle = 0
  AnglePitch = 0
  AngleRoll = 0
  Disabled = true
  Group = -> [ElementLink054,ElementLink055]
  LockAngle = false
  Multiply = false
  _ConstraintType = 36
  _Parent = -> Constraints
FEATURE [App::FeaturePython] ElementLink054  label="_Element051"  # link proxy (typed FeaturePython)
  LinkTransform = true
  LinkedObject = -> _Element051
  _Parent = -> Constraint029
FEATURE [Part::FeaturePython] _Element051  # link proxy (typed FeaturePython)
  Detach = false
  LinkTransform = true
  LinkedObject = -> Link008 [BaseFeature.Edge7]
  _Parent = -> Elements
FEATURE [App::FeaturePython] ElementLink055  label="_Element052"  # link proxy (typed FeaturePython)
  LinkTransform = true
  LinkedObject = -> _Element052
  _Parent = -> Constraint029
FEATURE [Part::FeaturePython] _Element052  # link proxy (typed FeaturePython)
  Detach = false
  LinkTransform = true
  LinkedObject = -> Link006 [BaseFeature.Edge17]
  _Parent = -> Elements
FEATURE [App::FeaturePython] Constraint030  label="PlaneCoincident007"  # WARN: FeaturePython — macro-defined, semantics opaque (R4)
  Angle = 0
  AnglePitch = 0
  AngleRoll = 0
  Cascade = false
  Disabled = false
  Group = -> [ElementLink056,ElementLink057]
  LockAngle = false
  Multiply = false
  OffsetX = 0
  OffsetY = 0
  _ConstraintType = 35
  _Parent = -> Constraints
FEATURE [App::FeaturePython] ElementLink056  label="_Element052"  # link proxy (typed FeaturePython)
  LinkTransform = true
  LinkedObject = -> _Element052
  _Parent = -> Constraint030
FEATURE [App::FeaturePython] ElementLink057  label="_Element051"  # link proxy (typed FeaturePython)
  LinkTransform = true
  LinkedObject = -> _Element051
  _Parent = -> Constraint030
FEATURE [App::FeaturePython] Constraint031  label="Locked006"  # WARN: FeaturePython — macro-defined, semantics opaque (R4)
  Disabled = false
  Group = -> [ElementLink058]
  _ConstraintType = 0
  _Parent = -> Constraints
FEATURE [App::FeaturePython] ElementLink058  label="_Element053"  # link proxy (typed FeaturePython)
  LinkTransform = true
  LinkedObject = -> _Element053
  _Parent = -> Constraint031
FEATURE [Part::FeaturePython] _Element053  # link proxy (typed FeaturePython)
  Detach = false
  LinkTransform = true
  LinkedObject = -> Link008 [BaseFeature.Face5]
  _Parent = -> Elements
FEATURE [App::FeaturePython] Constraint032  label="AxialAlignment015"  # WARN: FeaturePython — macro-defined, semantics opaque (R4)
  Angle = 0
  AnglePitch = 0
  AngleRoll = 0
  Disabled = true
  Group = -> [ElementLink059,ElementLink060]
  LockAngle = false
  Multiply = false
  _ConstraintType = 36
  _Parent = -> Constraints
FEATURE [App::FeaturePython] ElementLink059  label="_Element054"  # link proxy (typed FeaturePython)
  LinkTransform = true
  LinkedObject = -> _Element054
  _Parent = -> Constraint032
FEATURE [Part::FeaturePython] _Element054  # link proxy (typed FeaturePython)
  Detach = false
  LinkTransform = true
  LinkedObject = -> Link008 [BaseFeature.Edge240]
  _Parent = -> Elements
FEATURE [App::FeaturePython] ElementLink060  label="_Element055"  # link proxy (typed FeaturePython)
  LinkTransform = true
  LinkedObject = -> _Element055
  _Parent = -> Constraint032
FEATURE [Part::FeaturePython] _Element055  # link proxy (typed FeaturePython)
  Detach = false
  LinkTransform = true
  LinkedObject = -> Link009 [BaseFeature.Edge218]
  _Parent = -> Elements
FEATURE [App::FeaturePython] Constraint033  label="AxialAlignment016"  # WARN: FeaturePython — macro-defined, semantics opaque (R4)
  Angle = 0
  AnglePitch = 0
  AngleRoll = 0
  Disabled = true
  Group = -> [ElementLink061,ElementLink062]
  LockAngle = false
  Multiply = false
  _ConstraintType = 36
  _Parent = -> Constraints
FEATURE [App::FeaturePython] ElementLink061  label="_Element056"  # link proxy (typed FeaturePython)
  LinkTransform = true
  LinkedObject = -> _Element056
  _Parent = -> Constraint033
FEATURE [Part::FeaturePython] _Element056  # link proxy (typed FeaturePython)
  Detach = false
  LinkTransform = true
  LinkedObject = -> Link009 [BaseFeature.Edge198]
  _Parent = -> Elements
FEATURE [App::FeaturePython] ElementLink062  label="_Element057"  # link proxy (typed FeaturePython)
  LinkTransform = true
  LinkedObject = -> _Element057
  _Parent = -> Constraint033
FEATURE [Part::FeaturePython] _Element057  # link proxy (typed FeaturePython)
  Detach = false
  LinkTransform = true
  LinkedObject = -> Link008 [BaseFeature.Edge228]
  _Parent = -> Elements
FEATURE [App::FeaturePython] Constraint034  label="PlaneCoincident008"  # WARN: FeaturePython — macro-defined, semantics opaque (R4)
  Angle = 0
  AnglePitch = 0
  AngleRoll = 0
  Cascade = false
  Disabled = false
  Group = -> [ElementLink063,ElementLink064]
  LockAngle = false
  Multiply = false
  OffsetX = 0
  OffsetY = 0
  _ConstraintType = 35
  _Parent = -> Constraints
FEATURE [App::FeaturePython] ElementLink063  label="_Element057"  # link proxy (typed FeaturePython)
  LinkTransform = true
  LinkedObject = -> _Element057
  _Parent = -> Constraint034
FEATURE [App::FeaturePython] ElementLink064  label="_Element056"  # link proxy (typed FeaturePython)
  LinkTransform = true
  LinkedObject = -> _Element056
  _Parent = -> Constraint034
FEATURE [App::FeaturePython] Constraint035  label="Locked007"  # WARN: FeaturePython — macro-defined, semantics opaque (R4)
  Disabled = false
  Group = -> [ElementLink065]
  _ConstraintType = 0
  _Parent = -> Constraints
FEATURE [App::FeaturePython] ElementLink065  label="_Element058"  # link proxy (typed FeaturePython)
  LinkTransform = true
  LinkedObject = -> _Element058
  _Parent = -> Constraint035
FEATURE [Part::FeaturePython] _Element058  # link proxy (typed FeaturePython)
  Detach = false
  LinkTransform = true
  LinkedObject = -> Link009 [BaseFeature.Face5]
  _Parent = -> Elements
FEATURE [Part::FeaturePython] Assembly001  label="Circle Assembly"  # WARN: FeaturePython — macro-defined, semantics opaque (R4)
  AutoRelax = true
  BuildShape = 0
  Freeze = false
  Group = -> [Constraints001,Elements001,Parts001]
  Verbose = false
  _SolverType = 1
  _Version = 1
FEATURE [App::FeaturePython] Constraints001  # WARN: FeaturePython — macro-defined, semantics opaque (R4)
  Group = -> [Constraint036,Constraint037,Constraint038,Constraint039,Constraint040,Constraint041,Constraint042,Constraint043,Constraint044,Constraint045,Constraint046,Constraint047,Constraint048,Constraint049,Constraint050,Constraint051,Constraint052]
  _Version = 1
FEATURE [App::FeaturePython] Elements001  # WARN: FeaturePython — macro-defined, semantics opaque (R4)
  Group = -> [_Element059,_Element060,_Element061,_Element062,_Element063,_Element064,_Element065,_Element066,_Element067,_Element068,_Element069,_Element070,_Element071,_Element072,_Element073,_Element074,_Element075,_Element076,_Element077,_Element078,_Element079,Element,Element003]
FEATURE [App::FeaturePython] Constraint036  label="AxialAlignment017"  # WARN: FeaturePython — macro-defined, semantics opaque (R4)
  Angle = 0
  AnglePitch = 0
  AngleRoll = 0
  Disabled = true
  Group = -> [ElementLink066,ElementLink067]
  LockAngle = false
  Multiply = false
  _ConstraintType = 36
  _Parent = -> Constraints001
FEATURE [App::FeaturePython] ElementLink066  label="_Element059"  # link proxy (typed FeaturePython)
  LinkTransform = true
  LinkedObject = -> _Element059
  _Parent = -> Constraint036
FEATURE [Part::FeaturePython] _Element059  # link proxy (typed FeaturePython)
  Detach = false
  LinkTransform = true
  LinkedObject = -> Link011 [BaseFeature.Edge17]
  _Parent = -> Elements001
FEATURE [App::FeaturePython] ElementLink067  label="_Element060"  # link proxy (typed FeaturePython)
  LinkTransform = true
  LinkedObject = -> _Element060
  _Parent = -> Constraint036
FEATURE [Part::FeaturePython] _Element060  # link proxy (typed FeaturePython)
  Detach = false
  LinkTransform = true
  LinkedObject = -> Link010 [BaseFeature.Edge240]
  _Parent = -> Elements001
FEATURE [App::FeaturePython] Constraint037  label="AxialAlignment018"  # WARN: FeaturePython — macro-defined, semantics opaque (R4)
  Angle = 0
  AnglePitch = 0
  AngleRoll = 0
  Disabled = true
  Group = -> [ElementLink068,ElementLink069]
  LockAngle = false
  Multiply = false
  _ConstraintType = 36
  _Parent = -> Constraints001
FEATURE [App::FeaturePython] ElementLink068  label="_Element061"  # link proxy (typed FeaturePython)
  LinkTransform = true
  LinkedObject = -> _Element061
  _Parent = -> Constraint037
FEATURE [Part::FeaturePython] _Element061  # link proxy (typed FeaturePython)
  Detach = false
  LinkTransform = true
  LinkedObject = -> Link010 [BaseFeature.Edge228]
  _Parent = -> Elements001
FEATURE [App::FeaturePython] ElementLink069  label="_Element062"  # link proxy (typed FeaturePython)
  LinkTransform = true
  LinkedObject = -> _Element062
  _Parent = -> Constraint037
FEATURE [Part::FeaturePython] _Element062  # link proxy (typed FeaturePython)
  Detach = false
  LinkTransform = true
  LinkedObject = -> Link011 [BaseFeature.Edge7]
  _Parent = -> Elements001
FEATURE [App::FeaturePython] Constraint038  label="PlaneCoincident009"  # WARN: FeaturePython — macro-defined, semantics opaque (R4)
  Angle = 0
  AnglePitch = 0
  AngleRoll = 0
  Cascade = false
  Disabled = false
  Group = -> [ElementLink070,ElementLink071]
  LockAngle = false
  Multiply = false
  OffsetX = 0
  OffsetY = 0
  _ConstraintType = 35
  _Parent = -> Constraints001
FEATURE [App::FeaturePython] ElementLink070  label="_Element060"  # link proxy (typed FeaturePython)
  LinkTransform = true
  LinkedObject = -> _Element060
  _Parent = -> Constraint038
FEATURE [App::FeaturePython] ElementLink071  label="_Element059"  # link proxy (typed FeaturePython)
  LinkTransform = true
  LinkedObject = -> _Element059
  _Parent = -> Constraint038
FEATURE [App::FeaturePython] Constraint039  label="Locked008"  # WARN: FeaturePython — macro-defined, semantics opaque (R4)
  Disabled = false
  Group = -> [ElementLink072]
  _ConstraintType = 0
  _Parent = -> Constraints001
FEATURE [App::FeaturePython] ElementLink072  label="_Element063"  # link proxy (typed FeaturePython)
  LinkTransform = true
  LinkedObject = -> _Element063
  _Parent = -> Constraint039
FEATURE [Part::FeaturePython] _Element063  # link proxy (typed FeaturePython)
  Detach = false
  LinkTransform = true
  LinkedObject = -> Link010 [BaseFeature.Face5]
  _Parent = -> Elements001
FEATURE [App::FeaturePython] Constraint040  label="Locked009"  # WARN: FeaturePython — macro-defined, semantics opaque (R4)
  Disabled = false
  Group = -> [ElementLink073]
  _ConstraintType = 0
  _Parent = -> Constraints001
FEATURE [App::FeaturePython] ElementLink073  label="_Element064"  # link proxy (typed FeaturePython)
  LinkTransform = true
  LinkedObject = -> _Element064
  _Parent = -> Constraint040
FEATURE [Part::FeaturePython] _Element064  # link proxy (typed FeaturePython)
  Detach = false
  LinkTransform = true
  LinkedObject = -> Link011 [BaseFeature.Face5]
  _Parent = -> Elements001
FEATURE [Part::FeaturePython] _Element065  # link proxy (typed FeaturePython)
  Detach = false
  LinkTransform = true
  LinkedObject = -> Link012 [BaseFeature.Edge240]
  _Parent = -> Elements001
FEATURE [App::FeaturePython] Constraint041  label="AxialAlignment019"  # WARN: FeaturePython — macro-defined, semantics opaque (R4)
  Angle = 0
  AnglePitch = 0
  AngleRoll = 0
  Disabled = true
  Group = -> [ElementLink074,ElementLink075]
  LockAngle = false
  Multiply = false
  _ConstraintType = 36
  _Parent = -> Constraints001
FEATURE [App::FeaturePython] ElementLink074  label="_Element065"  # link proxy (typed FeaturePython)
  LinkTransform = true
  LinkedObject = -> _Element065
  _Parent = -> Constraint041
FEATURE [App::FeaturePython] ElementLink075  label="_Element066"  # link proxy (typed FeaturePython)
  LinkTransform = true
  LinkedObject = -> _Element066
  _Parent = -> Constraint041
FEATURE [Part::FeaturePython] _Element066  # link proxy (typed FeaturePython)
  Detach = false
  LinkTransform = true
  LinkedObject = -> Link010 [BaseFeature.Edge17]
  _Parent = -> Elements001
FEATURE [App::FeaturePython] Constraint042  label="AxialAlignment020"  # WARN: FeaturePython — macro-defined, semantics opaque (R4)
  Angle = 0
  AnglePitch = 0
  AngleRoll = 0
  Disabled = true
  Group = -> [ElementLink076,ElementLink077]
  LockAngle = false
  Multiply = false
  _ConstraintType = 36
  _Parent = -> Constraints001
FEATURE [App::FeaturePython] ElementLink076  label="_Element067"  # link proxy (typed FeaturePython)
  LinkTransform = true
  LinkedObject = -> _Element067
  _Parent = -> Constraint042
FEATURE [Part::FeaturePython] _Element067  # link proxy (typed FeaturePython)
  Detach = false
  LinkTransform = true
  LinkedObject = -> Link012 [BaseFeature.Edge228]
  _Parent = -> Elements001
FEATURE [App::FeaturePython] ElementLink077  label="_Element068"  # link proxy (typed FeaturePython)
  LinkTransform = true
  LinkedObject = -> _Element068
  _Parent = -> Constraint042
FEATURE [Part::FeaturePython] _Element068  # link proxy (typed FeaturePython)
  Detach = false
  LinkTransform = true
  LinkedObject = -> Link010 [BaseFeature.Edge7]
  _Parent = -> Elements001
FEATURE [App::FeaturePython] Constraint043  label="PlaneCoincident010"  # WARN: FeaturePython — macro-defined, semantics opaque (R4)
  Angle = 0
  AnglePitch = 0
  AngleRoll = 0
  Cascade = false
  Disabled = false
  Group = -> [ElementLink078,ElementLink079]
  LockAngle = false
  Multiply = false
  OffsetX = 0
  OffsetY = 0
  _ConstraintType = 35
  _Parent = -> Constraints001
FEATURE [App::FeaturePython] ElementLink078  label="_Element068"  # link proxy (typed FeaturePython)
  LinkTransform = true
  LinkedObject = -> _Element068
  _Parent = -> Constraint043
FEATURE [App::FeaturePython] ElementLink079  label="_Element067"  # link proxy (typed FeaturePython)
  LinkTransform = true
  LinkedObject = -> _Element067
  _Parent = -> Constraint043
FEATURE [App::FeaturePython] Constraint044  label="Locked010"  # WARN: FeaturePython — macro-defined, semantics opaque (R4)
  Disabled = false
  Group = -> [ElementLink080]
  _ConstraintType = 0
  _Parent = -> Constraints001
FEATURE [App::FeaturePython] ElementLink080  label="_Element069"  # link proxy (typed FeaturePython)
  LinkTransform = true
  LinkedObject = -> _Element069
  _Parent = -> Constraint044
FEATURE [Part::FeaturePython] _Element069  # link proxy (typed FeaturePython)
  Detach = false
  LinkTransform = true
  LinkedObject = -> Link012 [BaseFeature.Face5]
  _Parent = -> Elements001
FEATURE [App::FeaturePython] Constraint045  label="AxialAlignment021"  # WARN: FeaturePython — macro-defined, semantics opaque (R4)
  Angle = 0
  AnglePitch = 0
  AngleRoll = 0
  Disabled = true
  Group = -> [ElementLink081,ElementLink082]
  LockAngle = false
  Multiply = false
  _ConstraintType = 36
  _Parent = -> Constraints001
FEATURE [App::FeaturePython] ElementLink081  label="_Element070"  # link proxy (typed FeaturePython)
  LinkTransform = true
  LinkedObject = -> _Element070
  _Parent = -> Constraint045
FEATURE [Part::FeaturePython] _Element070  # link proxy (typed FeaturePython)
  Detach = false
  LinkTransform = true
  LinkedObject = -> Link013 [BaseFeature.Edge198]
  _Parent = -> Elements001
FEATURE [App::FeaturePython] ElementLink082  label="_Element071"  # link proxy (typed FeaturePython)
  LinkTransform = true
  LinkedObject = -> _Element071
  _Parent = -> Constraint045
FEATURE [Part::FeaturePython] _Element071  # link proxy (typed FeaturePython)
  Detach = false
  LinkTransform = true
  LinkedObject = -> Link012 [BaseFeature.Edge17]
  _Parent = -> Elements001
FEATURE [App::FeaturePython] Constraint046  label="AxialAlignment022"  # WARN: FeaturePython — macro-defined, semantics opaque (R4)
  Angle = 0
  AnglePitch = 0
  AngleRoll = 0
  Disabled = true
  Group = -> [ElementLink083,ElementLink084]
  LockAngle = false
  Multiply = false
  _ConstraintType = 36
  _Parent = -> Constraints001
FEATURE [App::FeaturePython] ElementLink083  label="_Element072"  # link proxy (typed FeaturePython)
  LinkTransform = true
  LinkedObject = -> _Element072
  _Parent = -> Constraint046
FEATURE [Part::FeaturePython] _Element072  # link proxy (typed FeaturePython)
  Detach = false
  LinkTransform = true
  LinkedObject = -> Link013 [BaseFeature.Edge218]
  _Parent = -> Elements001
FEATURE [App::FeaturePython] ElementLink084  label="_Element073"  # link proxy (typed FeaturePython)
  LinkTransform = true
  LinkedObject = -> _Element073
  _Parent = -> Constraint046
FEATURE [Part::FeaturePython] _Element073  # link proxy (typed FeaturePython)
  Detach = false
  LinkTransform = true
  LinkedObject = -> Link012 [BaseFeature.Edge7]
  _Parent = -> Elements001
FEATURE [App::FeaturePython] Constraint047  label="PlaneCoincident011"  # WARN: FeaturePython — macro-defined, semantics opaque (R4)
  Angle = 0
  AnglePitch = 0
  AngleRoll = 0
  Cascade = false
  Disabled = false
  Group = -> [ElementLink085,ElementLink086]
  LockAngle = false
  Multiply = false
  OffsetX = 0
  OffsetY = 0
  _ConstraintType = 35
  _Parent = -> Constraints001
FEATURE [App::FeaturePython] ElementLink085  label="_Element071"  # link proxy (typed FeaturePython)
  LinkTransform = true
  LinkedObject = -> _Element071
  _Parent = -> Constraint047
FEATURE [App::FeaturePython] ElementLink086  label="_Element070"  # link proxy (typed FeaturePython)
  LinkTransform = true
  LinkedObject = -> _Element070
  _Parent = -> Constraint047
FEATURE [App::FeaturePython] Constraint048  label="Locked011"  # WARN: FeaturePython — macro-defined, semantics opaque (R4)
  Disabled = false
  Group = -> [ElementLink087]
  _ConstraintType = 0
  _Parent = -> Constraints001
FEATURE [App::FeaturePython] ElementLink087  label="_Element074"  # link proxy (typed FeaturePython)
  LinkTransform = true
  LinkedObject = -> _Element074
  _Parent = -> Constraint048
FEATURE [Part::FeaturePython] _Element074  # link proxy (typed FeaturePython)
  Detach = false
  LinkTransform = true
  LinkedObject = -> Link013 [BaseFeature.Face5]
  _Parent = -> Elements001
FEATURE [App::FeaturePython] Constraint049  label="AxialAlignment023"  # WARN: FeaturePython — macro-defined, semantics opaque (R4)
  Angle = 0
  AnglePitch = 0
  AngleRoll = 0
  Disabled = true
  Group = -> [ElementLink088,ElementLink089]
  LockAngle = false
  Multiply = false
  _ConstraintType = 36
  _Parent = -> Constraints001
FEATURE [App::FeaturePython] ElementLink088  label="_Element075"  # link proxy (typed FeaturePython)
  LinkTransform = true
  LinkedObject = -> _Element075
  _Parent = -> Constraint049
FEATURE [Part::FeaturePython] _Element075  # link proxy (typed FeaturePython)
  Detach = false
  LinkTransform = true
  LinkedObject = -> Link014 [BaseFeature.Edge17]
  _Parent = -> Elements001
FEATURE [App::FeaturePython] ElementLink089  label="_Element076"  # link proxy (typed FeaturePython)
  LinkTransform = true
  LinkedObject = -> _Element076
  _Parent = -> Constraint049
FEATURE [Part::FeaturePython] _Element076  # link proxy (typed FeaturePython)
  Detach = false
  LinkTransform = true
  LinkedObject = -> Link013 [BaseFeature.Edge240]
  _Parent = -> Elements001
FEATURE [App::FeaturePython] Constraint050  label="AxialAlignment024"  # WARN: FeaturePython — macro-defined, semantics opaque (R4)
  Angle = 0
  AnglePitch = 0
  AngleRoll = 0
  Disabled = true
  Group = -> [ElementLink090,ElementLink091]
  LockAngle = false
  Multiply = false
  _ConstraintType = 36
  _Parent = -> Constraints001
FEATURE [App::FeaturePython] ElementLink090  label="_Element077"  # link proxy (typed FeaturePython)
  LinkTransform = true
  LinkedObject = -> _Element077
  _Parent = -> Constraint050
FEATURE [Part::FeaturePython] _Element077  # link proxy (typed FeaturePython)
  Detach = false
  LinkTransform = true
  LinkedObject = -> Link014 [BaseFeature.Edge7]
  _Parent = -> Elements001
FEATURE [App::FeaturePython] ElementLink091  label="_Element078"  # link proxy (typed FeaturePython)
  LinkTransform = true
  LinkedObject = -> _Element078
  _Parent = -> Constraint050
FEATURE [Part::FeaturePython] _Element078  # link proxy (typed FeaturePython)
  Detach = false
  LinkTransform = true
  LinkedObject = -> Link013 [BaseFeature.Edge228]
  _Parent = -> Elements001
FEATURE [App::FeaturePython] Constraint051  label="PlaneCoincident012"  # WARN: FeaturePython — macro-defined, semantics opaque (R4)
  Angle = 0
  AnglePitch = 0
  AngleRoll = 0
  Cascade = false
  Disabled = false
  Group = -> [ElementLink092,ElementLink093]
  LockAngle = false
  Multiply = false
  OffsetX = 0
  OffsetY = 0
  _ConstraintType = 35
  _Parent = -> Constraints001
FEATURE [App::FeaturePython] ElementLink092  label="_Element075"  # link proxy (typed FeaturePython)
  LinkTransform = true
  LinkedObject = -> _Element075
  _Parent = -> Constraint051
FEATURE [App::FeaturePython] ElementLink093  label="_Element076"  # link proxy (typed FeaturePython)
  LinkTransform = true
  LinkedObject = -> _Element076
  _Parent = -> Constraint051
FEATURE [App::FeaturePython] Constraint052  label="Locked012"  # WARN: FeaturePython — macro-defined, semantics opaque (R4)
  Disabled = false
  Group = -> [ElementLink094]
  _ConstraintType = 0
  _Parent = -> Constraints001
FEATURE [App::FeaturePython] ElementLink094  label="_Element079"  # link proxy (typed FeaturePython)
  LinkTransform = true
  LinkedObject = -> _Element079
  _Parent = -> Constraint052
FEATURE [Part::FeaturePython] _Element079  # link proxy (typed FeaturePython)
  Detach = false
  LinkTransform = true
  LinkedObject = -> Link014 [BaseFeature.Face5]
  _Parent = -> Elements001
FEATURE [Part::FeaturePython] Assembly002  label="Ring Circle Assembly"  # WARN: FeaturePython — macro-defined, semantics opaque (R4)
  AutoRelax = true
  BuildShape = 0
  Freeze = false
  Group = -> [Constraints002,Elements002,Parts002]
  Verbose = false
  _SolverType = 1
  _Version = 1
FEATURE [App::FeaturePython] Constraints002  # WARN: FeaturePython — macro-defined, semantics opaque (R4)
  Group = -> [Constraint053,Constraint054,Constraint055]
  _Version = 1
FEATURE [App::FeaturePython] Elements002  # WARN: FeaturePython — macro-defined, semantics opaque (R4)
  Group = -> [_Element080,_Element081,_Element082,_Element083]
FEATURE [App::FeaturePython] Constraint053  label="AxialAlignment025"  # WARN: FeaturePython — macro-defined, semantics opaque (R4)
  Angle = 0
  AnglePitch = 0
  AngleRoll = 0
  Disabled = true
  Group = -> [ElementLink095,ElementLink096]
  LockAngle = false
  Multiply = false
  _ConstraintType = 36
  _Parent = -> Constraints002
FEATURE [App::FeaturePython] ElementLink095  label="_Element080"  # link proxy (typed FeaturePython)
  LinkTransform = true
  LinkedObject = -> _Element080
  _Parent = -> Constraint053
FEATURE [Part::FeaturePython] Element  # link proxy (typed FeaturePython)
  Detach = false
  LinkTransform = true
  LinkedObject = -> Link012 [BaseFeature.Edge218]
  _Parent = -> Elements001
FEATURE [Part::FeaturePython] _Element080  # link proxy (typed FeaturePython)
  Detach = false
  LinkTransform = true
  LinkedObject = -> Link016 [1.$Element.]
  _Parent = -> Elements002
FEATURE [App::FeaturePython] ElementLink096  label="_Element081"  # link proxy (typed FeaturePython)
  LinkTransform = true
  LinkedObject = -> _Element081
  _Parent = -> Constraint053
FEATURE [Part::FeaturePython] Element001  # link proxy (typed FeaturePython)
  Detach = false
  LinkTransform = true
  LinkedObject = -> Link004 [BaseFeature.Edge240]
  _Parent = -> Elements
FEATURE [Part::FeaturePython] _Element081  # link proxy (typed FeaturePython)
  Detach = false
  LinkTransform = true
  LinkedObject = -> Link015 [1.$Element001.]
  _Parent = -> Elements002
FEATURE [App::FeaturePython] Constraint054  label="AxialAlignment026"  # WARN: FeaturePython — macro-defined, semantics opaque (R4)
  Angle = 0
  AnglePitch = 0
  AngleRoll = 0
  Disabled = true
  Group = -> [ElementLink097,ElementLink098]
  LockAngle = false
  Multiply = false
  _ConstraintType = 36
  _Parent = -> Constraints002
FEATURE [App::FeaturePython] ElementLink097  label="_Element082"  # link proxy (typed FeaturePython)
  LinkTransform = true
  LinkedObject = -> _Element082
  _Parent = -> Constraint054
FEATURE [Part::FeaturePython] Element002  # link proxy (typed FeaturePython)
  Detach = false
  LinkTransform = true
  LinkedObject = -> Link004 [BaseFeature.Edge239]
  _Parent = -> Elements
FEATURE [Part::FeaturePython] _Element082  # link proxy (typed FeaturePython)
  Detach = false
  LinkTransform = true
  LinkedObject = -> Link015 [1.$Element002.]
  _Parent = -> Elements002
FEATURE [App::FeaturePython] ElementLink098  label="_Element083"  # link proxy (typed FeaturePython)
  LinkTransform = true
  LinkedObject = -> _Element083
  _Parent = -> Constraint054
FEATURE [Part::FeaturePython] Element003  # link proxy (typed FeaturePython)
  Detach = false
  LinkTransform = true
  LinkedObject = -> Link012 [BaseFeature.Edge208]
  _Parent = -> Elements001
FEATURE [Part::FeaturePython] _Element083  # link proxy (typed FeaturePython)
  Detach = false
  LinkTransform = true
  LinkedObject = -> Link016 [1.$Element003.]
  _Parent = -> Elements002
FEATURE [App::FeaturePython] Constraint055  label="PlaneCoincident013"  # WARN: FeaturePython — macro-defined, semantics opaque (R4)
  Angle = 0
  AnglePitch = 0
  AngleRoll = 0
  Cascade = false
  Disabled = false
  Group = -> [ElementLink099,ElementLink100]
  LockAngle = false
  Multiply = false
  OffsetX = 0
  OffsetY = 0
  _ConstraintType = 35
  _Parent = -> Constraints002
FEATURE [App::FeaturePython] ElementLink099  label="_Element080"  # link proxy (typed FeaturePython)
  LinkTransform = true
  LinkedObject = -> _Element080
  _Parent = -> Constraint055
FEATURE [App::FeaturePython] ElementLink100  label="_Element081"  # link proxy (typed FeaturePython)
  LinkTransform = true
  LinkedObject = -> _Element081
  _Parent = -> Constraint055
